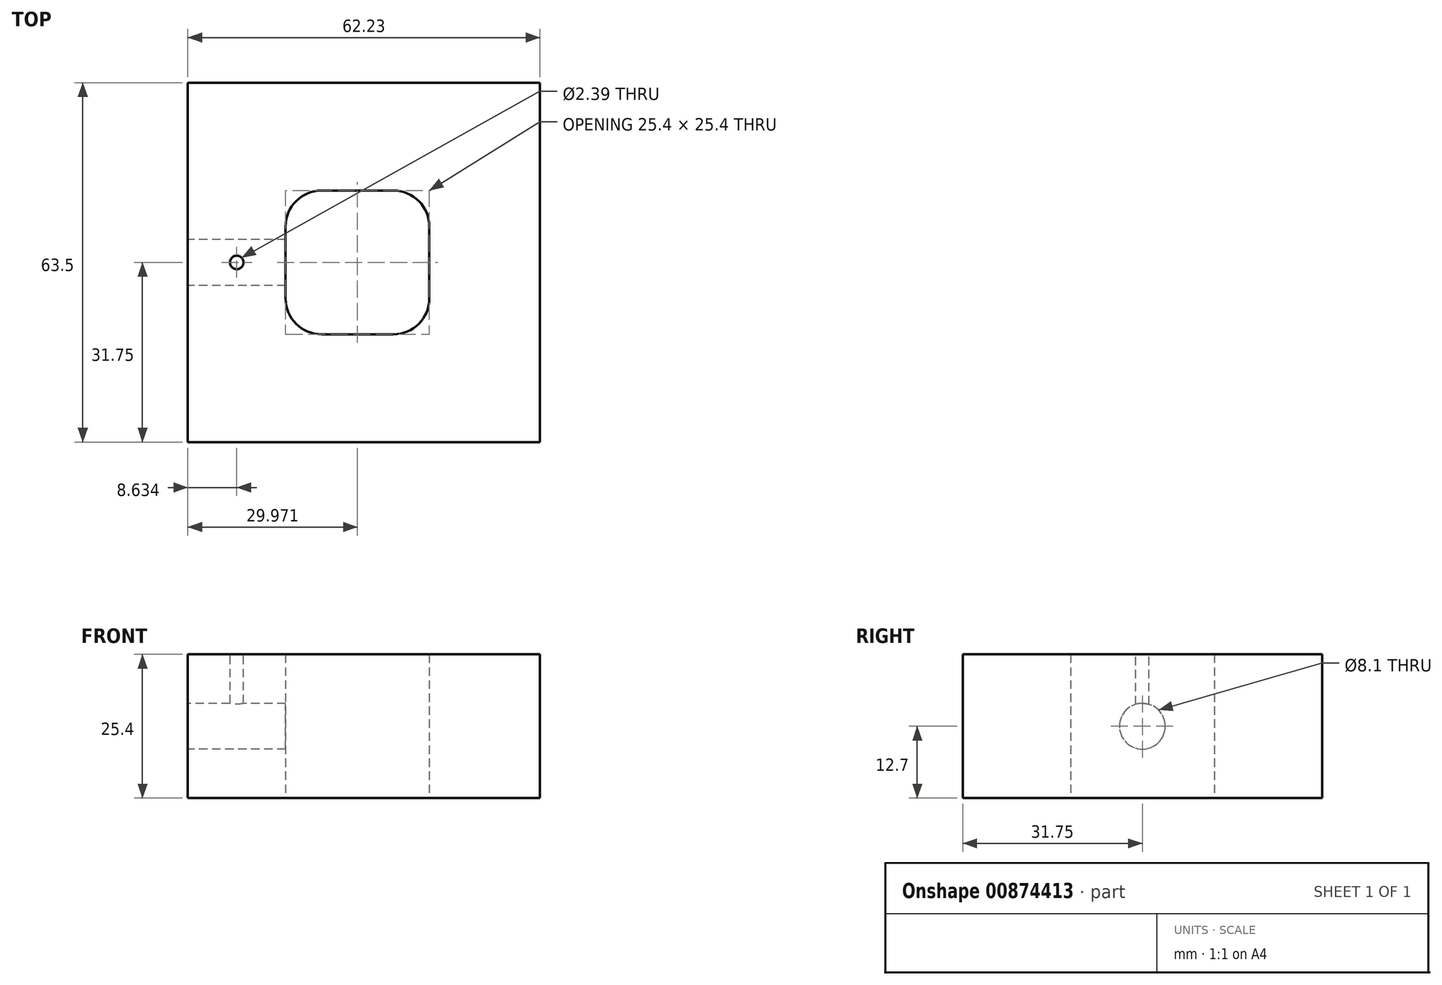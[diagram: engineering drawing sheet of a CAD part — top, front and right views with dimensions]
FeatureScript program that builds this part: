
annotation { "Feature Type Name" : "Feature", "Feature Type Description" : "" }
export const myFeature = defineFeature(function(context is Context, id is Id, definition is map)
    precondition{}
    {
        {
            var Q0;
            Q0=qCreatedBy(makeId("Top.planeOp"),FACE);
            var sketch = newSketch(context, id + "F0", { "sketchPlane" : qUnion([Q0])});
            skLineSegment(sketch, "E0.bottom", {"start": v(-29.27, 44.45) * mm, "end": v(32.96, 44.45) * mm});
            skLineSegment(sketch, "E0.top", {"start": v(-29.27, -19.05) * mm, "end": v(32.96, -19.05) * mm});
            skLineSegment(sketch, "E0.left", {"start": v(-29.27, 44.45) * mm, "end": v(-29.27, -19.05) * mm});
            skLineSegment(sketch, "E0.right", {"start": v(32.96, 44.45) * mm, "end": v(32.96, -19.05) * mm});
            skLineSegment(sketch, "E1.bottom", {"start": v(-5.65, 25.4) * mm, "end": v(7.05, 25.4) * mm});
            skLineSegment(sketch, "E1.top", {"start": v(-5.65, 0) * mm, "end": v(7.05, 0) * mm});
            skLineSegment(sketch, "E1.left", {"start": v(-12, 19.05) * mm, "end": v(-12, 6.35) * mm});
            skLineSegment(sketch, "E1.right", {"start": v(13.4, 19.05) * mm, "end": v(13.4, 6.35) * mm});
            skPoint(sketch, "E2.visualSharp", {"position": v(-12, 25.4) * mm});
            skArc(sketch, "E2.filletArc", {"start": v(-5.65, 25.4) * mm, "mid": v(-10.14, 23.54) * mm, "end": v(-12, 19.05) * mm});
            skPoint(sketch, "E3.visualSharp", {"position": v(-12, 0) * mm});
            skArc(sketch, "E3.filletArc", {"start": v(-12, 6.35) * mm, "mid": v(-10.14, 1.86) * mm, "end": v(-5.65, 0) * mm});
            skPoint(sketch, "E4.visualSharp", {"position": v(13.4, 0) * mm});
            skArc(sketch, "E4.filletArc", {"start": v(7.05, 0) * mm, "mid": v(11.54, 1.86) * mm, "end": v(13.4, 6.35) * mm});
            skPoint(sketch, "E5.visualSharp", {"position": v(13.4, 25.4) * mm});
            skArc(sketch, "E5.filletArc", {"start": v(13.4, 19.05) * mm, "mid": v(11.54, 23.54) * mm, "end": v(7.05, 25.4) * mm});
            skSolve(sketch);
        }
        {
            var Q0;
            Q0=makeQuery(id+"F0.imprint","IMPRINT",FACE,{"disambiguationData":[TD([[makeQuery(id+"F0.imprint","IMPRINT",EDGE,{"derivedFrom":sQuery(id+"F0.wireOp",EDGE,"E0.bottom")}),-1.0]])]});
            extrude(context, id + "F1", {"entities" : qUnion([Q0]), "depth" : 25.4 * mm, "offsetDistance" : 25.4 * mm});
        }
        {
            var Q0;
            Q0=makeQuery(id+"F1.opExtrude","SWEPT_FACE",FACE,{"disambiguationData":[OSD([sQuery(id+"F0.wireOp",EDGE,"E0.left")])]});
            var sketch = newSketch(context, id + "F2", { "sketchPlane" : qUnion([Q0])});
            skCircle(sketch, "E6", {"center": v(-12.7, 12.7) * mm, "radius": 4.05 * mm});
            skSolve(sketch);
        }
        {
            var Q0;
            Q0=sQuery(id+"F2.wireOp",VERTEX,"E6.center");
            var Q1;
            Q1=makeQuery(id+"F1.opExtrude","SWEPT_BODY",BODY,{"disambiguationData":[OSD([sQuery(id+"F0.wireOp",EDGE,"E0.bottom"),sQuery(id+"F0.wireOp",EDGE,"E0.top"),sQuery(id+"F0.wireOp",EDGE,"E0.left"),sQuery(id+"F0.wireOp",EDGE,"E0.right"),sQuery(id+"F0.wireOp",EDGE,"E1.bottom"),sQuery(id+"F0.wireOp",EDGE,"E1.top"),sQuery(id+"F0.wireOp",EDGE,"E1.left"),sQuery(id+"F0.wireOp",EDGE,"E1.right"),sQuery(id+"F0.wireOp",EDGE,"E2.filletArc"),sQuery(id+"F0.wireOp",EDGE,"E3.filletArc"),sQuery(id+"F0.wireOp",EDGE,"E4.filletArc"),sQuery(id+"F0.wireOp",EDGE,"E5.filletArc")])]});
            hole(context, id + "F3", {"style" : HoleStyle.SIMPLE, "endStyle" : HoleEndStyle.BLIND, "holeDiameter" : 8.1 * mm, "majorDiameter" : 6.35 * mm, "holeDepth" : 20.32 * mm, "isTappedThrough" : true, "tappedDepth" : 12.7 * mm, "tapClearance" : 3, "startFromSketch" : true, "locations" : qUnion([Q0]), "scope" : qUnion([Q1])});
        }
        {
            var Q0;
            Q0=makeQuery(id+"F1.opExtrude","CAP_FACE",FACE,{"disambiguationData":[OSD([sQuery(id+"F0.wireOp",EDGE,"E0.bottom"),sQuery(id+"F0.wireOp",EDGE,"E0.top"),sQuery(id+"F0.wireOp",EDGE,"E0.left"),sQuery(id+"F0.wireOp",EDGE,"E0.right"),sQuery(id+"F0.wireOp",EDGE,"E1.bottom"),sQuery(id+"F0.wireOp",EDGE,"E1.top"),sQuery(id+"F0.wireOp",EDGE,"E1.left"),sQuery(id+"F0.wireOp",EDGE,"E1.right"),sQuery(id+"F0.wireOp",EDGE,"E2.filletArc"),sQuery(id+"F0.wireOp",EDGE,"E3.filletArc"),sQuery(id+"F0.wireOp",EDGE,"E4.filletArc"),sQuery(id+"F0.wireOp",EDGE,"E5.filletArc")])],"isStart":false});
            var sketch = newSketch(context, id + "F4", { "sketchPlane" : qUnion([Q0])});
            skCircle(sketch, "E7", {"center": v(-20.64, 12.7) * mm, "radius": 1.2 * mm});
            skSolve(sketch);
        }
        {
            var Q0;
            Q0=sQuery(id+"F4.wireOp",VERTEX,"E7.center");
            var Q1;
            Q1=makeQuery(id+"F1.opExtrude","SWEPT_BODY",BODY,{"disambiguationData":[OSD([sQuery(id+"F0.wireOp",EDGE,"E0.bottom"),sQuery(id+"F0.wireOp",EDGE,"E0.top"),sQuery(id+"F0.wireOp",EDGE,"E0.left"),sQuery(id+"F0.wireOp",EDGE,"E0.right"),sQuery(id+"F0.wireOp",EDGE,"E1.bottom"),sQuery(id+"F0.wireOp",EDGE,"E1.top"),sQuery(id+"F0.wireOp",EDGE,"E1.left"),sQuery(id+"F0.wireOp",EDGE,"E1.right"),sQuery(id+"F0.wireOp",EDGE,"E2.filletArc"),sQuery(id+"F0.wireOp",EDGE,"E3.filletArc"),sQuery(id+"F0.wireOp",EDGE,"E4.filletArc"),sQuery(id+"F0.wireOp",EDGE,"E5.filletArc")])]});
            hole(context, id + "F5", {"style" : HoleStyle.SIMPLE, "endStyle" : HoleEndStyle.BLIND, "holeDiameter" : 2.4 * mm, "majorDiameter" : 6.35 * mm, "holeDepth" : 12.7 * mm, "isTappedThrough" : true, "tappedDepth" : 12.7 * mm, "tapClearance" : 3, "startFromSketch" : true, "locations" : qUnion([Q0]), "scope" : qUnion([Q1])});
        }
    });
